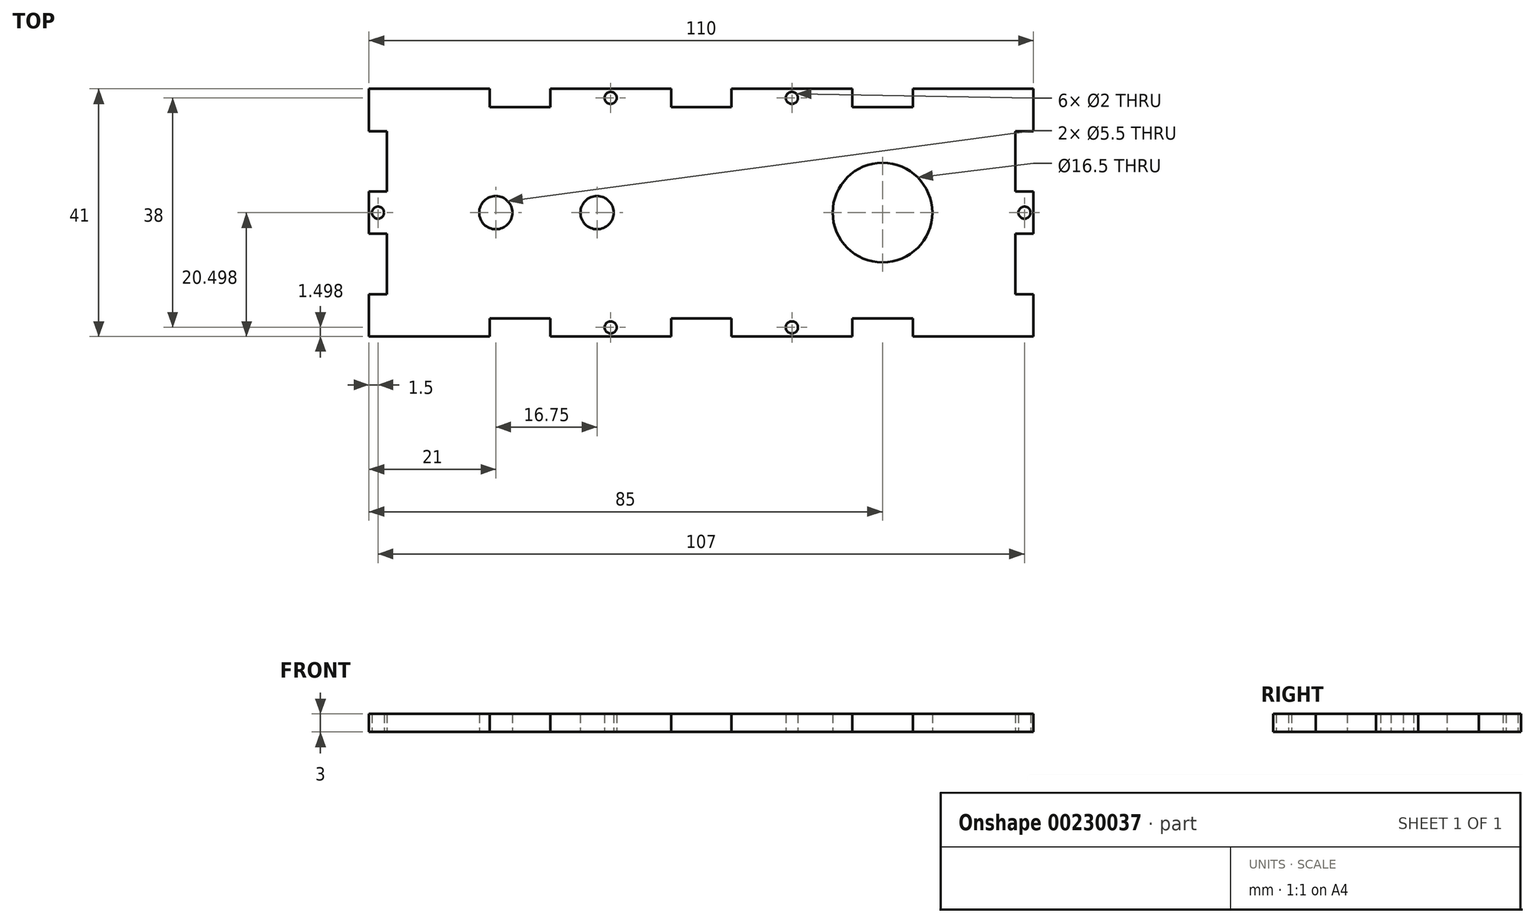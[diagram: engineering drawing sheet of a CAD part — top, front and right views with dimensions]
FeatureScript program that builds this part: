
annotation { "Feature Type Name" : "Feature", "Feature Type Description" : "" }
export const myFeature = defineFeature(function(context is Context, id is Id, definition is map)
    precondition{}
    {
        {
            var Q0;
            Q0=qCreatedBy(makeId("Top.planeOp"),FACE);
            var sketch = newSketch(context, id + "F0", { "sketchPlane" : qUnion([Q0])});
            skLineSegment(sketch, "E0", {"start": v(-55, 21.1) * mm, "end": v(-55, 14.1) * mm});
            skLineSegment(sketch, "E1", {"start": v(-55, 14.1) * mm, "end": v(-52, 14.1) * mm});
            skLineSegment(sketch, "E2", {"start": v(-52, 14.1) * mm, "end": v(-52, 4.1) * mm});
            skLineSegment(sketch, "E3", {"start": v(-52, 4.1) * mm, "end": v(-55, 4.1) * mm});
            skLineSegment(sketch, "E4", {"start": v(-55, 4.1) * mm, "end": v(-55, 0.6) * mm});
            skLineSegment(sketch, "E5", {"start": v(-55, 21.1) * mm, "end": v(-35, 21.1) * mm});
            skLineSegment(sketch, "E6", {"start": v(-35, 21.1) * mm, "end": v(-35, 18.1) * mm});
            skLineSegment(sketch, "E7", {"start": v(-35, 18.1) * mm, "end": v(-25, 18.1) * mm});
            skLineSegment(sketch, "E8", {"start": v(-25, 18.1) * mm, "end": v(-25, 21.1) * mm});
            skLineSegment(sketch, "E9", {"start": v(-25, 21.1) * mm, "end": v(-5, 21.1) * mm});
            skLineSegment(sketch, "E10", {"start": v(-5, 21.1) * mm, "end": v(-5, 18.1) * mm});
            skLineSegment(sketch, "E11", {"start": v(-5, 18.1) * mm, "end": v(0, 18.1) * mm});
            skLineSegment(sketch, "E12", {"start": v(-55, 0.6) * mm, "end": v(0, 0.6) * mm, "construction": true});
            skLineSegment(sketch, "E13.MirrorCS", {"start": v(-55, -12.9) * mm, "end": v(-52, -12.9) * mm});
            skLineSegment(sketch, "E14.MirrorCS", {"start": v(-25, -16.9) * mm, "end": v(-25, -19.9) * mm});
            skLineSegment(sketch, "E15.MirrorCS", {"start": v(-52, -2.9) * mm, "end": v(-55, -2.9) * mm});
            skLineSegment(sketch, "E16.MirrorCS", {"start": v(-55, -2.9) * mm, "end": v(-55, 0.6) * mm});
            skLineSegment(sketch, "E17.MirrorCS", {"start": v(-35, -19.9) * mm, "end": v(-35, -16.9) * mm});
            skLineSegment(sketch, "E18.MirrorCS", {"start": v(-5, -19.9) * mm, "end": v(-5, -16.9) * mm});
            skLineSegment(sketch, "E19.MirrorCS", {"start": v(-55, -19.9) * mm, "end": v(-55, -12.9) * mm});
            skLineSegment(sketch, "E20.MirrorCS", {"start": v(-5, -16.9) * mm, "end": v(0, -16.9) * mm});
            skLineSegment(sketch, "E21.MirrorCS", {"start": v(-52, -12.9) * mm, "end": v(-52, -2.9) * mm});
            skLineSegment(sketch, "E22.MirrorCS", {"start": v(-25, -19.9) * mm, "end": v(-5, -19.9) * mm});
            skLineSegment(sketch, "E23.MirrorCS", {"start": v(-55, -19.9) * mm, "end": v(-35, -19.9) * mm});
            skLineSegment(sketch, "E24.MirrorCS", {"start": v(-35, -16.9) * mm, "end": v(-25, -16.9) * mm});
            skLineSegment(sketch, "E25", {"start": v(0, 18.1) * mm, "end": v(0, -16.9) * mm, "construction": true});
            skLineSegment(sketch, "E26.MirrorCS", {"start": v(55, -2.9) * mm, "end": v(55, 0.6) * mm});
            skLineSegment(sketch, "E27.MirrorCS", {"start": v(5, 21.1) * mm, "end": v(5, 18.1) * mm});
            skLineSegment(sketch, "E28.MirrorCS", {"start": v(25, 18.1) * mm, "end": v(25, 21.1) * mm});
            skLineSegment(sketch, "E29.MirrorCS", {"start": v(35, 21.1) * mm, "end": v(35, 18.1) * mm});
            skLineSegment(sketch, "E30.MirrorCS", {"start": v(55, 4.1) * mm, "end": v(55, 0.6) * mm});
            skLineSegment(sketch, "E31.MirrorCS", {"start": v(52, 4.1) * mm, "end": v(55, 4.1) * mm});
            skLineSegment(sketch, "E32.MirrorCS", {"start": v(55, 14.1) * mm, "end": v(52, 14.1) * mm});
            skLineSegment(sketch, "E33.MirrorCS", {"start": v(25, -16.9) * mm, "end": v(25, -19.9) * mm});
            skLineSegment(sketch, "E34.MirrorCS", {"start": v(52, -2.9) * mm, "end": v(55, -2.9) * mm});
            skLineSegment(sketch, "E35.MirrorCS", {"start": v(5, -19.9) * mm, "end": v(5, -16.9) * mm});
            skLineSegment(sketch, "E36.MirrorCS", {"start": v(55, -12.9) * mm, "end": v(52, -12.9) * mm});
            skLineSegment(sketch, "E37.MirrorCS", {"start": v(35, -19.9) * mm, "end": v(35, -16.9) * mm});
            skLineSegment(sketch, "E38.MirrorCS", {"start": v(5, -16.9) * mm, "end": v(0, -16.9) * mm});
            skLineSegment(sketch, "E39.MirrorCS", {"start": v(55, -19.9) * mm, "end": v(35, -19.9) * mm});
            skLineSegment(sketch, "E40.MirrorCS", {"start": v(25, -19.9) * mm, "end": v(5, -19.9) * mm});
            skLineSegment(sketch, "E41.MirrorCS", {"start": v(55, 0.6) * mm, "end": v(0, 0.6) * mm, "construction": true});
            skLineSegment(sketch, "E42.MirrorCS", {"start": v(5, 18.1) * mm, "end": v(0, 18.1) * mm});
            skLineSegment(sketch, "E43.MirrorCS", {"start": v(25, 21.1) * mm, "end": v(5, 21.1) * mm});
            skLineSegment(sketch, "E44.MirrorCS", {"start": v(35, 18.1) * mm, "end": v(25, 18.1) * mm});
            skLineSegment(sketch, "E45.MirrorCS", {"start": v(55, 21.1) * mm, "end": v(35, 21.1) * mm});
            skLineSegment(sketch, "E46.MirrorCS", {"start": v(52, 14.1) * mm, "end": v(52, 4.1) * mm});
            skLineSegment(sketch, "E47.MirrorCS", {"start": v(55, 21.1) * mm, "end": v(55, 14.1) * mm});
            skLineSegment(sketch, "E48.MirrorCS", {"start": v(55, -19.9) * mm, "end": v(55, -12.9) * mm});
            skLineSegment(sketch, "E49.MirrorCS", {"start": v(52, -12.9) * mm, "end": v(52, -2.9) * mm});
            skLineSegment(sketch, "E50.MirrorCS", {"start": v(35, -16.9) * mm, "end": v(25, -16.9) * mm});
            skCircle(sketch, "E51", {"center": v(-15, 19.6) * mm, "radius": 1 * mm});
            skPoint(sketch, "E51.centerSnap0", {"position": v(-15, 21.1) * mm});
            skCircle(sketch, "E52.MirrorC", {"center": v(-15, -18.4) * mm, "radius": 1 * mm});
            skCircle(sketch, "E53", {"center": v(-53.5, 0.6) * mm, "radius": 1 * mm});
            skCircle(sketch, "E54.MirrorC", {"center": v(15, 19.6) * mm, "radius": 1 * mm});
            skCircle(sketch, "E55.MirrorC", {"center": v(15, -18.4) * mm, "radius": 1 * mm});
            skCircle(sketch, "E56.MirrorC", {"center": v(53.5, 0.6) * mm, "radius": 1 * mm});
            skLineSegment(sketch, "E57", {"start": v(30, 18.1) * mm, "end": v(30, -16.9) * mm, "construction": true});
            skCircle(sketch, "E58", {"center": v(30, 0.6) * mm, "radius": 8.25 * mm});
            skLineSegment(sketch, "E59", {"start": v(-55, 0.6) * mm, "end": v(-52, 0.6) * mm, "construction": true});
            skLineSegment(sketch, "E60", {"start": v(-52, 0.6) * mm, "end": v(-34, 0.6) * mm, "construction": true});
            skCircle(sketch, "E61", {"center": v(-34, 0.6) * mm, "radius": 2.75 * mm});
            skLineSegment(sketch, "E62", {"start": v(-31.25, 0.6) * mm, "end": v(-17.25, 0.6) * mm, "construction": true});
            skCircle(sketch, "E63", {"center": v(-17.25, 0.6) * mm, "radius": 2.75 * mm});
            skSolve(sketch);
        }
        {
            var Q0;
            Q0=qSketchRegion(id+"F0",true);
            extrude(context, id + "F1", {"entities" : qUnion([Q0]), "depth" : 3 * mm});
        }
    });
